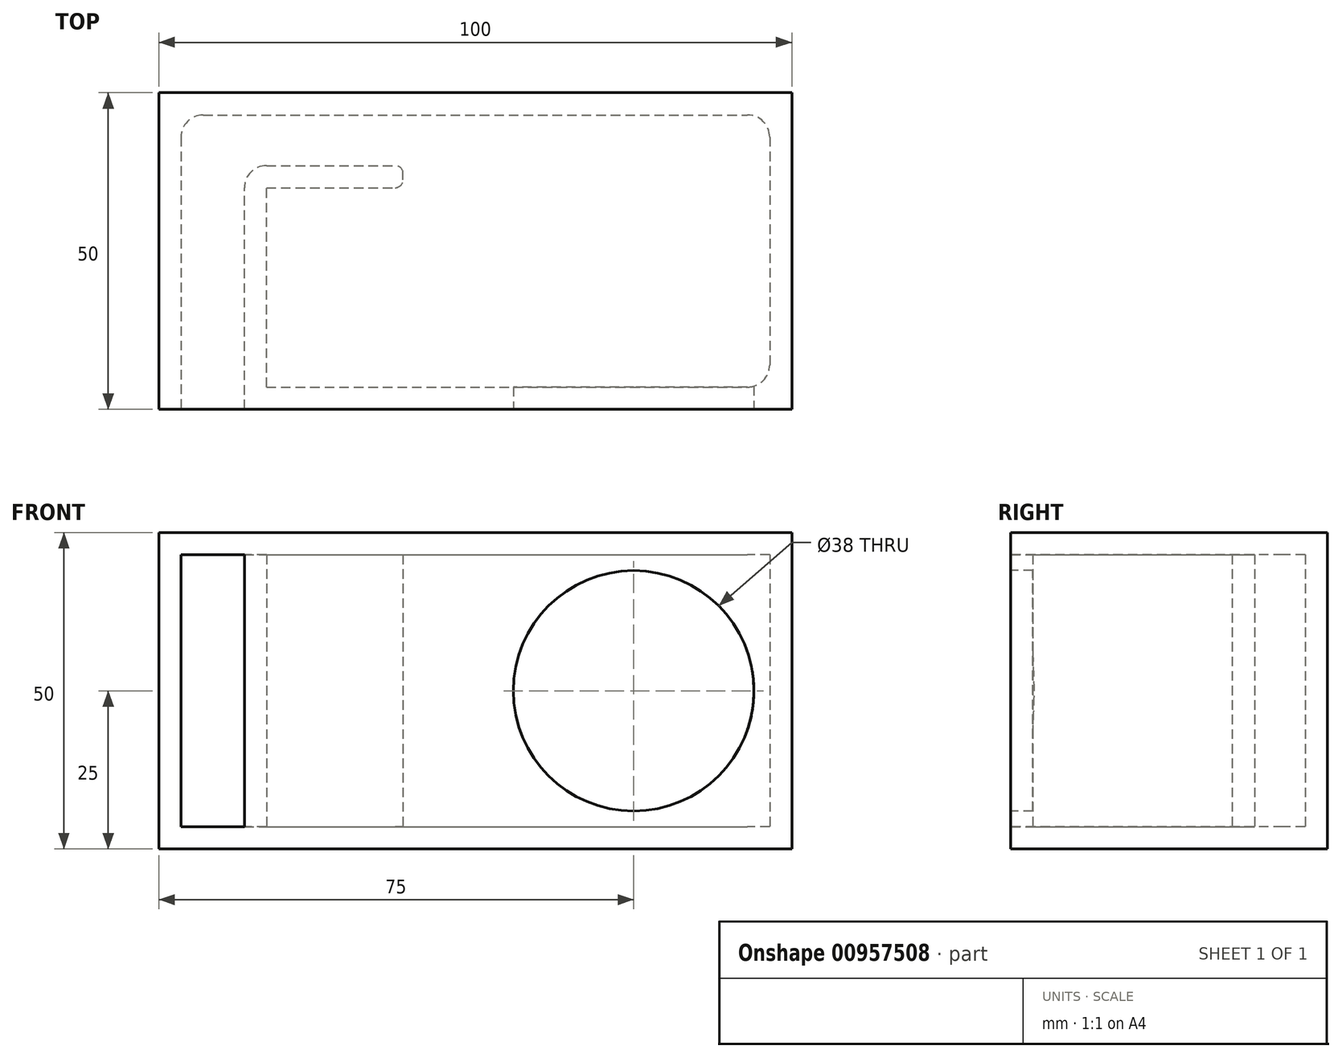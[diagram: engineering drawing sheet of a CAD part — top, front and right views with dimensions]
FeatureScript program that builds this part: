
annotation { "Feature Type Name" : "Feature", "Feature Type Description" : "" }
export const myFeature = defineFeature(function(context is Context, id is Id, definition is map)
    precondition{}
    {
        {
            var Q0;
            Q0=qCreatedBy(makeId("Top.planeOp"),FACE);
            var sketch = newSketch(context, id + "F0", { "sketchPlane" : qUnion([Q0])});
            skLineSegment(sketch, "E0.bottom", {"start": v(-100, 50) * mm, "end": v(0, 50) * mm});
            skLineSegment(sketch, "E0.top", {"start": v(-100, 0) * mm, "end": v(0, 0) * mm});
            skLineSegment(sketch, "E0.left", {"start": v(-100, 50) * mm, "end": v(-100, 0) * mm});
            skLineSegment(sketch, "E0.right", {"start": v(0, 50) * mm, "end": v(0, 0) * mm});
            skLineSegment(sketch, "E1.0", {"start": v(-3.5, 43) * mm, "end": v(-3.5, 7) * mm});
            skLineSegment(sketch, "E1.1", {"start": v(-93, 46.5) * mm, "end": v(-7, 46.5) * mm});
            skLineSegment(sketch, "E1.2", {"start": v(-96.5, 43) * mm, "end": v(-96.5, 3.5) * mm});
            skLineSegment(sketch, "E1.3", {"start": v(-96.5, 3.5) * mm, "end": v(-7, 3.5) * mm});
            skLineSegment(sketch, "E2", {"start": v(-86.5, 3.5) * mm, "end": v(-86.5, 35) * mm});
            skLineSegment(sketch, "E3", {"start": v(-83, 38.5) * mm, "end": v(-62.67, 38.5) * mm});
            skLineSegment(sketch, "E4.0", {"start": v(-83, 35) * mm, "end": v(-64.79, 35) * mm});
            skLineSegment(sketch, "E4.1", {"start": v(-83, 3) * mm, "end": v(-83, 35) * mm});
            skPoint(sketch, "E5.visualSharp", {"position": v(-96.5, 46.5) * mm});
            skArc(sketch, "E5.filletArc", {"start": v(-93, 46.5) * mm, "mid": v(-95.47, 45.47) * mm, "end": v(-96.5, 43) * mm});
            skPoint(sketch, "E6.visualSharp", {"position": v(-86.5, 38.5) * mm});
            skArc(sketch, "E6.filletArc", {"start": v(-83, 38.5) * mm, "mid": v(-85.47, 37.47) * mm, "end": v(-86.5, 35) * mm});
            skPoint(sketch, "E7.visualSharp", {"position": v(-3.5, 46.5) * mm});
            skArc(sketch, "E7.filletArc", {"start": v(-3.5, 43) * mm, "mid": v(-4.53, 45.47) * mm, "end": v(-7, 46.5) * mm});
            skPoint(sketch, "E8.visualSharp", {"position": v(-3.5, 3.5) * mm});
            skArc(sketch, "E8.filletArc", {"start": v(-7, 3.5) * mm, "mid": v(-4.53, 4.53) * mm, "end": v(-3.5, 7) * mm});
            skLineSegment(sketch, "E9", {"start": v(-64.79, 35) * mm, "end": v(-62.67, 35) * mm});
            skLineSegment(sketch, "E10", {"start": v(-61.42, 36.25) * mm, "end": v(-61.42, 37.25) * mm});
            skPoint(sketch, "E11.visualSharp", {"position": v(-61.42, 38.5) * mm});
            skArc(sketch, "E11.filletArc", {"start": v(-61.42, 37.25) * mm, "mid": v(-61.78, 38.13) * mm, "end": v(-62.67, 38.5) * mm});
            skPoint(sketch, "E12.visualSharp", {"position": v(-61.42, 35) * mm});
            skArc(sketch, "E12.filletArc", {"start": v(-62.67, 35) * mm, "mid": v(-61.78, 35.37) * mm, "end": v(-61.42, 36.25) * mm});
            skSolve(sketch);
        }
        {
            var Q0;
            Q0 = qSketchRegion(id + "F0", true);
            extrude(context, id + "F1", {"entities" : qUnion([Q0]), "depth" : 50 * mm, "offsetDistance" : 25 * mm});
        }
        {
            var Q0;
            Q0=makeQuery(id+"F0.imprint","IMPRINT",FACE,{"disambiguationData":[TD([[makeQuery(id+"F0.imprint","IMPRINT",EDGE,{"derivedFrom":sQuery(id+"F0.wireOp",EDGE,"E1.0")}),-1.0]])]});
            extrude(context, id + "F2", {"entities" : qUnion([Q0]), "operationType" : NewBodyOperationType.ADD, "depth" : 3.5 * mm, "offsetDistance" : 25 * mm});
        }
        {
            var Q0;
            Q0=makeQuery(id+"F0.imprint","IMPRINT",FACE,{"disambiguationData":[TD([[makeQuery(id+"F0.imprint","IMPRINT",EDGE,{"derivedFrom":sQuery(id+"F0.wireOp",EDGE,"E1.0")}),-1.0]])]});
            extrude(context, id + "F3", {"entities" : qUnion([Q0]), "operationType" : NewBodyOperationType.ADD, "depth" : 50 * mm, "offsetDistance" : 25 * mm, "hasSecondDirection" : true, "secondDirectionOppositeDirection" : false, "secondDirectionDepth" : 46.5 * mm});
        }
        {
            var Q0;
            Q0=qCreatedBy(makeId("Front.planeOp"),FACE);
            var sketch = newSketch(context, id + "F4", { "sketchPlane" : qUnion([Q0])});
            skCircle(sketch, "E13", {"center": v(-25, 25) * mm, "radius": 19 * mm});
            skLineSegment(sketch, "E14.bottom", {"start": v(-96.5, 46.5) * mm, "end": v(-86.5, 46.5) * mm});
            skLineSegment(sketch, "E14.top", {"start": v(-96.5, 3.5) * mm, "end": v(-86.5, 3.5) * mm});
            skLineSegment(sketch, "E14.left", {"start": v(-96.5, 46.5) * mm, "end": v(-96.5, 3.5) * mm});
            skLineSegment(sketch, "E14.right", {"start": v(-86.5, 46.5) * mm, "end": v(-86.5, 3.5) * mm});
            skSolve(sketch);
        }
        {
            var Q0;
            Q0=makeQuery(id+"F4.imprint","IMPRINT",FACE,{"disambiguationData":[TD([[makeQuery(id+"F4.imprint","IMPRINT",EDGE,{"derivedFrom":sQuery(id+"F4.wireOp",EDGE,"E14.bottom")}),-1.0]])]});
            var Q1;
            Q1=makeQuery(id+"F4.imprint","IMPRINT",FACE,{"disambiguationData":[TD([[makeQuery(id+"F4.imprint","IMPRINT",EDGE,{"derivedFrom":sQuery(id+"F4.wireOp",EDGE,"E13")}),1.0]])]});
            extrude(context, id + "F5", {"entities" : qUnion([Q0, Q1]), "operationType" : NewBodyOperationType.REMOVE, "oppositeDirection" : true, "depth" : 4 * mm, "offsetDistance" : 25 * mm});
        }
        {
            var Q0;
            {var subQ0=sQuery(id+"F0.wireOp",EDGE,"E2");Q0=makeQuery(id+"F0.imprint","IMPRINT",FACE,{"disambiguationData":[TD([[makeQuery(id+"F0.imprint","IMPRINT",EDGE,{"derivedFrom":subQ0}),-1.0]])]});}
            extrude(context, id + "F6", {"entities" : qUnion([Q0]), "operationType" : NewBodyOperationType.ADD, "depth" : 50 * mm, "offsetDistance" : 25 * mm});
        }
        {
            var Q0;
            Q0=makeQuery(id+"F0.imprint","IMPRINT",FACE,{"disambiguationData":[TD([[makeQuery(id+"F0.imprint","IMPRINT",EDGE,{"derivedFrom":sQuery(id+"F0.wireOp",EDGE,"E1.0")}),-1.0]])]});
            var Q1;
            {var subQ1=sQuery(id+"F0.wireOp",EDGE,"E2");Q1=makeQuery(id+"F0.imprint","IMPRINT",FACE,{"disambiguationData":[TD([[makeQuery(id+"F0.imprint","IMPRINT",EDGE,{"derivedFrom":subQ1}),-1.0]])]});}
            extrude(context, id + "F7", {"entities" : qUnion([Q0, Q1]), "operationType" : NewBodyOperationType.ADD, "depth" : 3.5 * mm, "offsetDistance" : 25 * mm});
        }
    });
